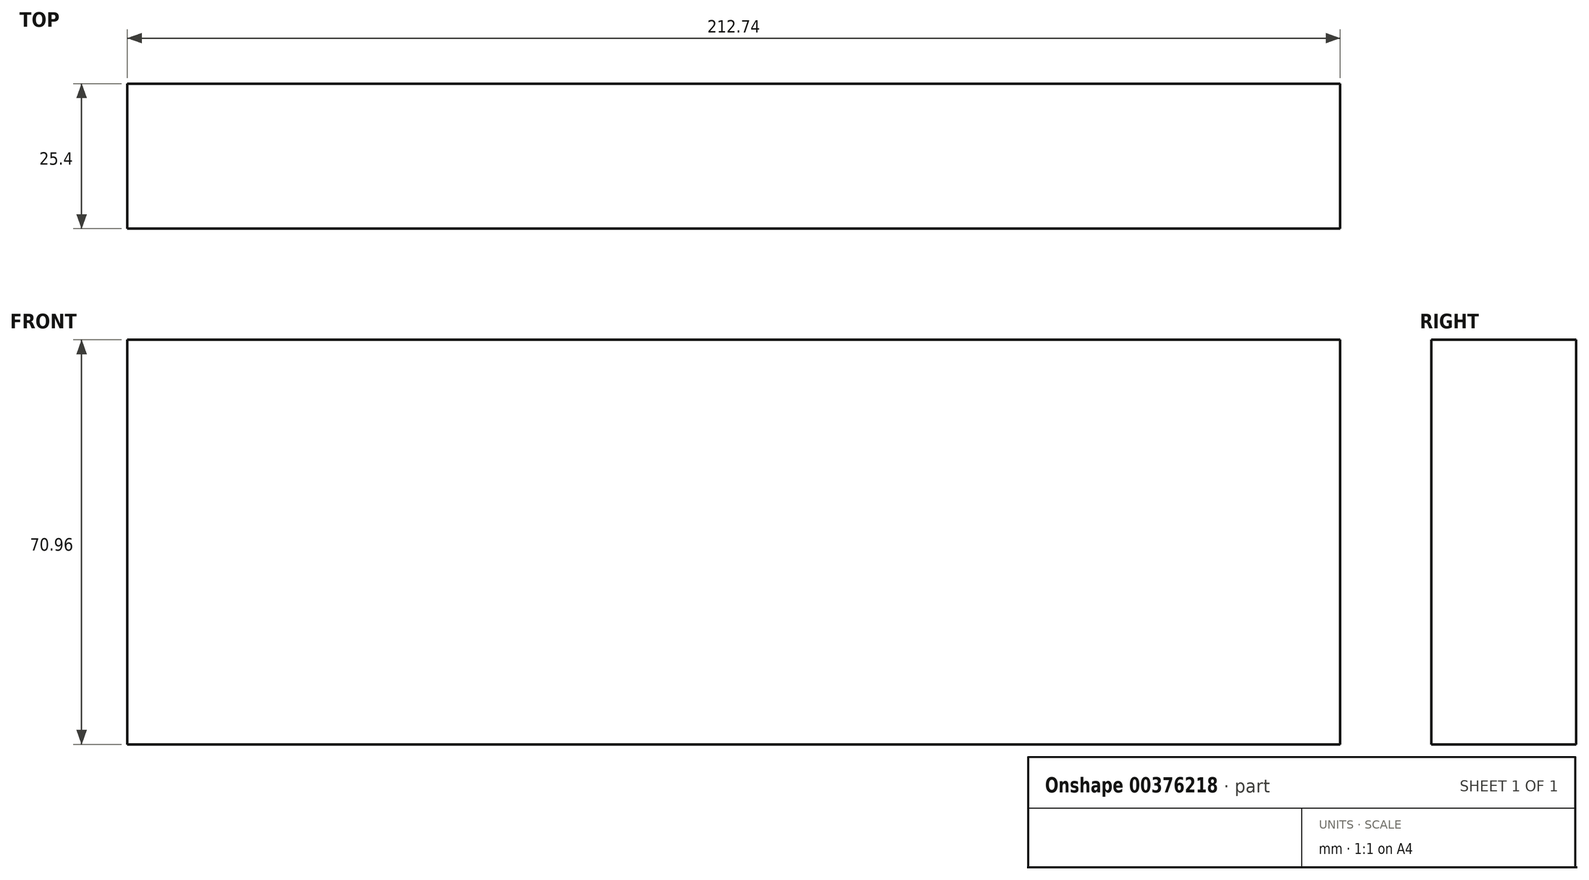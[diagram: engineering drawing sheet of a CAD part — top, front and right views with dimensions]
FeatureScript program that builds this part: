
annotation { "Feature Type Name" : "Feature", "Feature Type Description" : "" }
export const myFeature = defineFeature(function(context is Context, id is Id, definition is map)
    precondition{}
    {
        {
            var Q0;
            Q0=qCreatedBy(makeId("Front.planeOp"),FACE);
            var sketch = newSketch(context, id + "F0", { "sketchPlane" : qUnion([Q0])});
            skLineSegment(sketch, "E0.bottom", {"start": v(-106.37, 35.48) * mm, "end": v(106.37, 35.48) * mm});
            skLineSegment(sketch, "E0.top", {"start": v(-106.37, -35.48) * mm, "end": v(106.37, -35.48) * mm});
            skLineSegment(sketch, "E0.left", {"start": v(-106.37, 35.48) * mm, "end": v(-106.37, -35.48) * mm});
            skLineSegment(sketch, "E0.right", {"start": v(106.37, 35.48) * mm, "end": v(106.37, -35.48) * mm});
            skPoint(sketch, "E0.middle", {"position": v(0, 0) * mm});
            skSolve(sketch);
        }
        {
            var Q0;
            Q0 = qSketchRegion(id + "F0", true);
            extrude(context, id + "F1", {"entities" : qUnion([Q0]), "depth" : 25.4 * mm});
        }
    });
